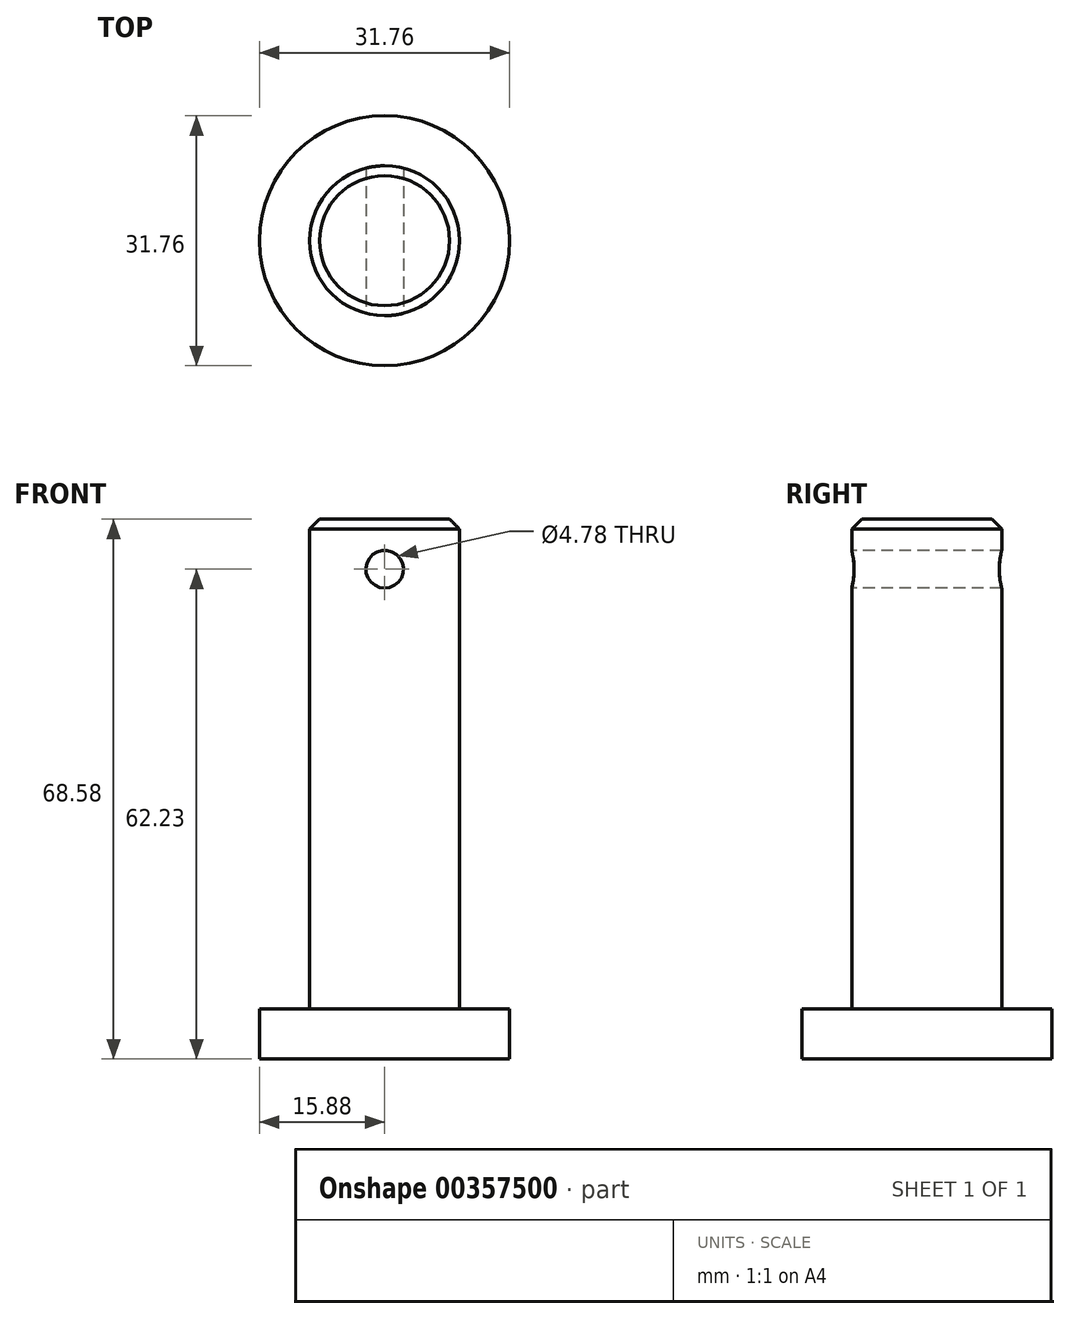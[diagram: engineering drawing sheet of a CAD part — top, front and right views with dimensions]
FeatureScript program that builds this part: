
annotation { "Feature Type Name" : "Feature", "Feature Type Description" : "" }
export const myFeature = defineFeature(function(context is Context, id is Id, definition is map)
    precondition{}
    {
        {
            var Q0;
            Q0=qCreatedBy(makeId("Top.planeOp"),FACE);
            var sketch = newSketch(context, id + "F0", { "sketchPlane" : qUnion([Q0])});
            skCircle(sketch, "E0", {"center": v(0, 0) * mm, "radius": 15.88 * mm});
            skCircle(sketch, "E1", {"center": v(0, 0) * mm, "radius": 9.53 * mm});
            skSolve(sketch);
        }
        {
            var Q0;
            Q0=makeQuery(id+"F0.imprint","IMPRINT",FACE,{"disambiguationData":[TD([[makeQuery(id+"F0.imprint","IMPRINT",EDGE,{"derivedFrom":sQuery(id+"F0.wireOp",EDGE,"E0")}),1.0]])]});
            var Q1;
            Q1=sQuery(id+"F0.wireOp",EDGE,"E0");
            var Q2;
            Q2=sQuery(id+"F0.wireOp",EDGE,"E1");
            extrude(context, id + "F1", {"entities" : qUnion([Q0]), "surfaceEntities" : qUnion([Q1, Q2]), "depth" : 6.35 * mm});
        }
        {
            var Q0;
            Q0=makeQuery(id+"F0.imprint","IMPRINT",FACE,{"disambiguationData":[TD([[makeQuery(id+"F0.imprint","IMPRINT",EDGE,{"derivedFrom":sQuery(id+"F0.wireOp",EDGE,"E1")}),1.0]])]});
            var Q1;
            Q1=sQuery(id+"F0.wireOp",EDGE,"E1");
            extrude(context, id + "F2", {"entities" : qUnion([Q0]), "operationType" : NewBodyOperationType.ADD, "surfaceEntities" : qUnion([Q1]), "depth" : 68.58 * mm});
        }
        {
            var Q0;
            Q0=qCreatedBy(makeId("Front.planeOp"),FACE);
            var sketch = newSketch(context, id + "F3", { "sketchPlane" : qUnion([Q0])});
            skCircle(sketch, "E2", {"center": v(0, 62.23) * mm, "radius": 2.39 * mm});
            skSolve(sketch);
        }
        {
            var Q0;
            Q0 = qSketchRegion(id + "F3", true);
            var Q1;
            Q1=sQuery(id+"F3.wireOp",EDGE,"E2");
            extrude(context, id + "F4", {"entities" : qUnion([Q0]), "operationType" : NewBodyOperationType.REMOVE, "surfaceEntities" : qUnion([Q1]), "endBound" : BoundingType.SYMMETRIC, "oppositeDirection" : true, "depth" : 127 * mm});
        }
        {
            var Q0;
            Q0=makeQuery(id+"F2.opExtrude","CAP_EDGE",EDGE,{"disambiguationData":[OSD([sQuery(id+"F0.wireOp",EDGE,"E1")])],"isStart":false});
            chamfer(context, id + "F5", {"entities" : qUnion([Q0]), "width" : 1.27 * mm, "tangentPropagation" : true});
        }
    });
